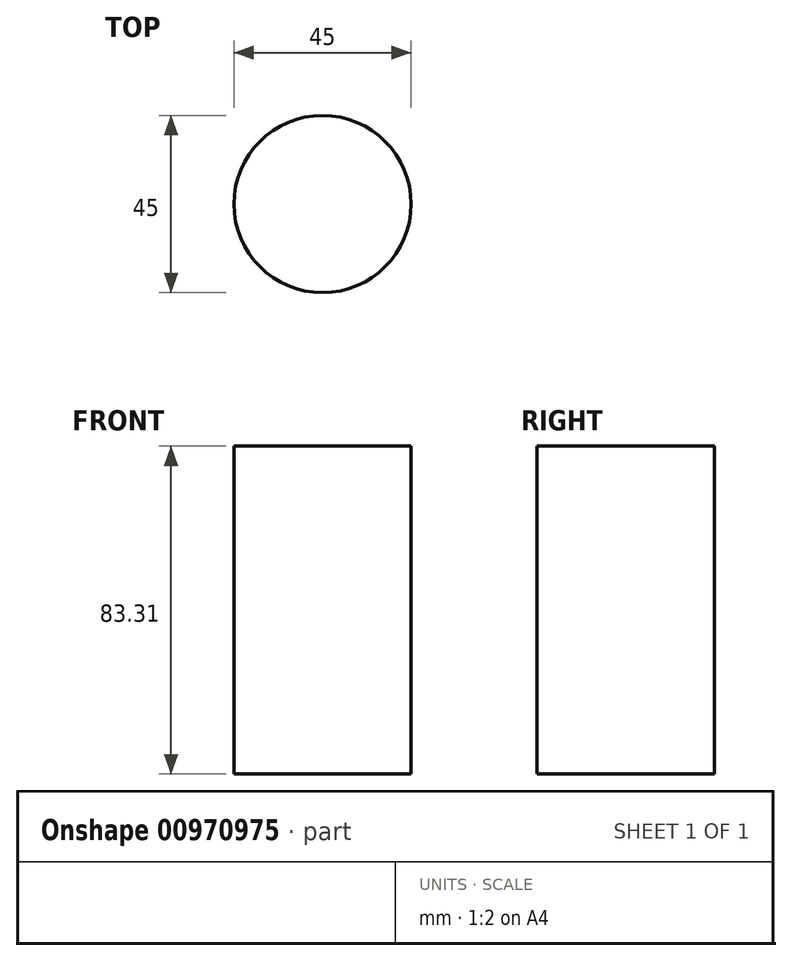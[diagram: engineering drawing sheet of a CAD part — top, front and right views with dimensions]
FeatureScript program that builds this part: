
annotation { "Feature Type Name" : "Feature", "Feature Type Description" : "" }
export const myFeature = defineFeature(function(context is Context, id is Id, definition is map)
    precondition{}
    {
        {
            var Q0;
            Q0=qCreatedBy(makeId("Top.planeOp"),FACE);
            var sketch = newSketch(context, id + "F0", { "sketchPlane" : qUnion([Q0])});
            skCircle(sketch, "E0", {"center": v(0, 0) * mm, "radius": 22.5 * mm});
            skSolve(sketch);
        }
        {
            var Q0;
            Q0 = qSketchRegion(id + "F0", true);
            extrude(context, id + "F1", {"entities" : qUnion([Q0]), "depth" : 83.31 * mm, "offsetDistance" : 25.4 * mm});
        }
    });
